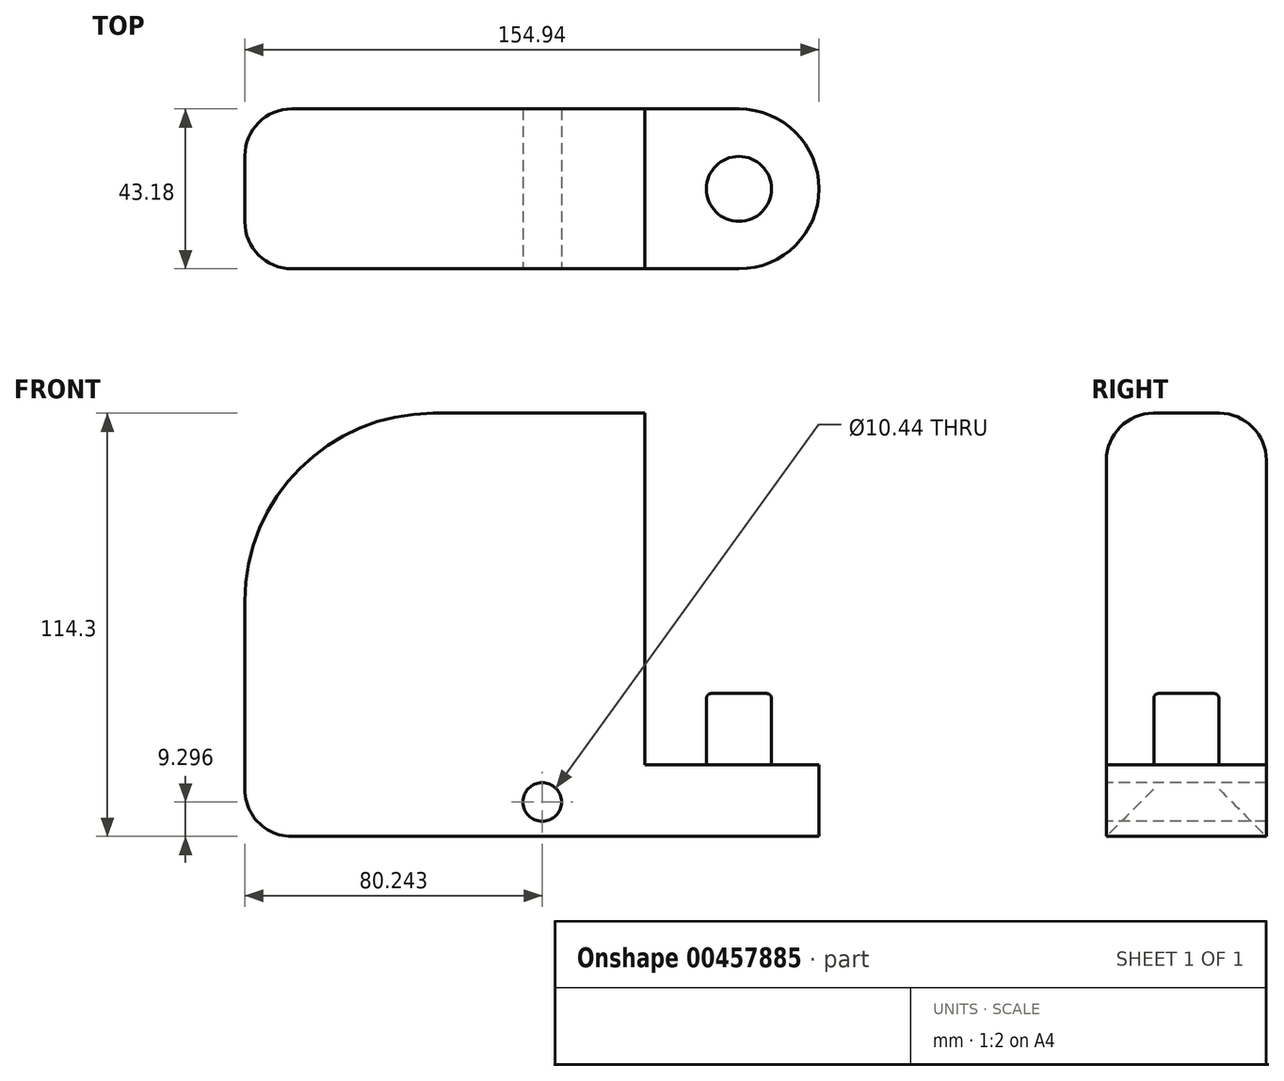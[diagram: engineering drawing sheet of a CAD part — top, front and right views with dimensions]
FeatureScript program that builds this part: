
annotation { "Feature Type Name" : "Feature", "Feature Type Description" : "" }
export const myFeature = defineFeature(function(context is Context, id is Id, definition is map)
    precondition{}
    {
        {
            var Q0;
            Q0=qCreatedBy(makeId("Front.planeOp"),FACE);
            var sketch = newSketch(context, id + "F0", { "sketchPlane" : qUnion([Q0])});
            skLineSegment(sketch, "E0.bottom", {"start": v(0, 0) * mm, "end": v(107.95, 0) * mm});
            skLineSegment(sketch, "E0.top", {"start": v(50.8, 114.3) * mm, "end": v(107.95, 114.3) * mm});
            skLineSegment(sketch, "E0.left", {"start": v(0, 0) * mm, "end": v(0, 63.5) * mm});
            skLineSegment(sketch, "E0.right", {"start": v(107.95, 0) * mm, "end": v(107.95, 114.3) * mm});
            skLineSegment(sketch, "E1.bottom", {"start": v(107.95, 0) * mm, "end": v(133.35, 0) * mm});
            skLineSegment(sketch, "E1.top", {"start": v(107.95, 19.3) * mm, "end": v(133.35, 19.3) * mm});
            skLineSegment(sketch, "E1.left", {"start": v(107.95, 0) * mm, "end": v(107.95, 19.3) * mm});
            skLineSegment(sketch, "E1.right", {"start": v(133.35, 0) * mm, "end": v(133.35, 19.3) * mm});
            skPoint(sketch, "E2.visualSharp", {"position": v(0, 114.3) * mm});
            skArc(sketch, "E2.filletArc", {"start": v(50.8, 114.3) * mm, "mid": v(14.88, 99.42) * mm, "end": v(0, 63.5) * mm});
            skSolve(sketch);
        }
        {
            var Q0;
            Q0=makeQuery(id+"F0.imprint","IMPRINT",FACE,{"disambiguationData":[TD([[makeQuery(id+"F0.imprint","IMPRINT",EDGE,{"derivedFrom":sQuery(id+"F0.wireOp",EDGE,"E0.bottom")}),1.0]])]});
            var Q1;
            Q1=makeQuery(id+"F0.imprint","IMPRINT",FACE,{"disambiguationData":[TD([[makeQuery(id+"F0.imprint","IMPRINT",EDGE,{"derivedFrom":sQuery(id+"F0.wireOp",EDGE,"E1.bottom")}),1.0]])]});
            extrude(context, id + "F1", {"entities" : qUnion([Q0, Q1]), "depth" : 43.18 * mm, "offsetDistance" : 25.4 * mm});
        }
        {
            var Q0;
            Q0=makeQuery(id+"F1.opExtrude","SWEPT_FACE",FACE,{"disambiguationData":[OSD([sQuery(id+"F0.wireOp",EDGE,"E1.top")])]});
            var sketch = newSketch(context, id + "F2", { "sketchPlane" : qUnion([Q0])});
            skArc(sketch, "E3", {"start": v(133.35, -43.18) * mm, "mid": v(154.94, -21.59) * mm, "end": v(133.35, 0) * mm});
            skSolve(sketch);
        }
        {
            var Q0;
            Q0 = qSketchRegion(id + "F2", true);
            var Q1;
            Q1=makeQuery(id+"F2.imprint","IMPRINT",FACE,{"disambiguationData":[TD([[makeQuery(id+"F2.imprint","IMPRINT",EDGE,{"derivedFrom":sQuery(id+"F2.wireOp",EDGE,"E3")}),1.0]])]});
            extrude(context, id + "F3", {"entities" : qUnion([Q0, Q1]), "operationType" : NewBodyOperationType.ADD, "oppositeDirection" : true, "depth" : 19.3 * mm, "offsetDistance" : 25.4 * mm});
        }
        {
            var Q0;
            {var subQ0=sQuery(id+"F0.wireOp",EDGE,"E1.top");Q0=makeQuery(id+"F3.boolean.opBoolean","MERGE",FACE,{"derivedFrom":[makeQuery(id+"F1.opExtrude","SWEPT_FACE",FACE,{"disambiguationData":[OSD([subQ0])]}),makeQuery(id+"F3.opExtrude","CAP_FACE",FACE,{"disambiguationData":[OSD([subQ0,sQuery(id+"F0.wireOp",EDGE,"E1.right"),sQuery(id+"F2.wireOp",EDGE,"E3")])],"isStart":true})]});}
            var sketch = newSketch(context, id + "F4", { "sketchPlane" : qUnion([Q0])});
            skLineSegment(sketch, "E4", {"start": v(107.95, -21.59) * mm, "end": v(154.94, -21.59) * mm, "construction": true});
            skLineSegment(sketch, "E5", {"start": v(133.35, 0) * mm, "end": v(133.35, -43.18) * mm, "construction": true});
            skCircle(sketch, "E6", {"center": v(133.35, -21.59) * mm, "radius": 8.76 * mm});
            skSolve(sketch);
        }
        {
            var Q0;
            Q0 = qSketchRegion(id + "F4", true);
            extrude(context, id + "F5", {"entities" : qUnion([Q0]), "operationType" : NewBodyOperationType.ADD, "depth" : 19.3 * mm, "offsetDistance" : 25.4 * mm});
        }
        {
            var Q0;
            Q0=makeQuery(id+"F5.opExtrude","CAP_FACE",FACE,{"disambiguationData":[OSD([sQuery(id+"F4.wireOp",EDGE,"E6")])],"isStart":false});
            fillet(context, id + "F6", {"entities" : qUnion([Q0]), "radius" : 1.27 * mm, "tangentPropagation" : true, "allowEdgeOverflow" : false});
        }
        {
            var Q0;
            Q0=makeQuery(id+"F1.opExtrude","SWEPT_FACE",FACE,{"disambiguationData":[OSD([sQuery(id+"F0.wireOp",EDGE,"E2.filletArc")])]});
            var Q1;
            Q1=makeQuery(id+"F1.opExtrude","SWEPT_EDGE",EDGE,{"disambiguationData":[OSD([sQuery(id+"F0.wireOp",EDGE,"E0.bottom"),sQuery(id+"F0.wireOp",EDGE,"E0.left")])]});
            fillet(context, id + "F7", {"entities" : qUnion([Q0, Q1]), "radius" : 12.7 * mm, "tangentPropagation" : true, "allowEdgeOverflow" : false});
        }
        {
            var Q0;
            Q0=makeQuery(id+"F1.opExtrude","CAP_FACE",FACE,{"disambiguationData":[OSD([sQuery(id+"F0.wireOp",EDGE,"E0.bottom"),sQuery(id+"F0.wireOp",EDGE,"E0.top"),sQuery(id+"F0.wireOp",EDGE,"E0.left"),sQuery(id+"F0.wireOp",EDGE,"E0.right"),sQuery(id+"F0.wireOp",EDGE,"E1.bottom"),sQuery(id+"F0.wireOp",EDGE,"E1.top"),sQuery(id+"F0.wireOp",EDGE,"E1.right"),sQuery(id+"F0.wireOp",EDGE,"E2.filletArc")])],"isStart":false});
            var sketch = newSketch(context, id + "F8", { "sketchPlane" : qUnion([Q0])});
            skLineSegment(sketch, "E7", {"start": v(12.7, 9.3) * mm, "end": v(133.35, 9.3) * mm, "construction": true});
            skCircle(sketch, "E8", {"center": v(80.24, 9.3) * mm, "radius": 5.22 * mm});
            skSolve(sketch);
        }
        {
            var Q0;
            Q0 = qSketchRegion(id + "F8", true);
            extrude(context, id + "F9", {"entities" : qUnion([Q0]), "operationType" : NewBodyOperationType.REMOVE, "endBound" : BoundingType.THROUGH_ALL, "oppositeDirection" : true, "depth" : 25.4 * mm, "offsetDistance" : 25.4 * mm});
        }
    });
